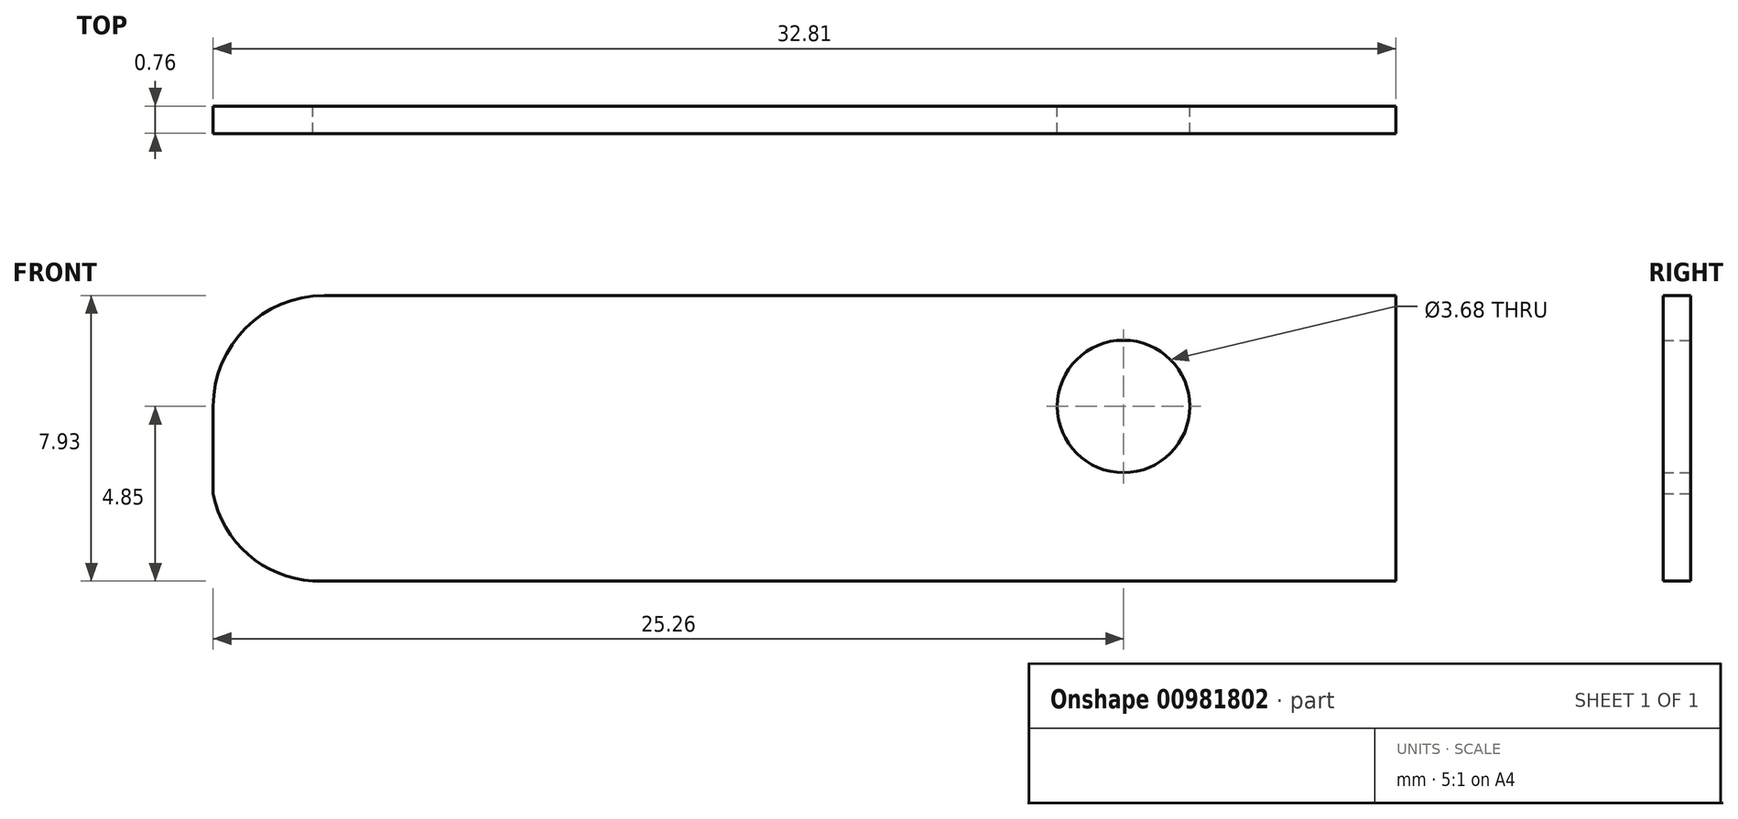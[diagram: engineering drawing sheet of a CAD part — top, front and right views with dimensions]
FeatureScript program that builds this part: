
annotation { "Feature Type Name" : "Feature", "Feature Type Description" : "" }
export const myFeature = defineFeature(function(context is Context, id is Id, definition is map)
    precondition{}
    {
        {
            var Q0;
            Q0=qCreatedBy(makeId("Front.planeOp"),FACE);
            var sketch = newSketch(context, id + "F0", { "sketchPlane" : qUnion([Q0])});
            skCircle(sketch, "E0", {"center": v(0, 0) * mm, "radius": 1.84 * mm});
            skLineSegment(sketch, "E1.bottom", {"start": v(-22.18, 3.08) * mm, "end": v(7.55, 3.08) * mm});
            skLineSegment(sketch, "E1.top", {"start": v(-22.49, -4.85) * mm, "end": v(7.55, -4.85) * mm});
            skLineSegment(sketch, "E1.left", {"start": v(-25.26, 0) * mm, "end": v(-25.26, -2.42) * mm});
            skLineSegment(sketch, "E1.right", {"start": v(7.55, 3.08) * mm, "end": v(7.55, -4.85) * mm});
            skArc(sketch, "E2", {"start": v(-22.18, 3.08) * mm, "mid": v(-24.36, 2.18) * mm, "end": v(-25.26, 0) * mm});
            skArc(sketch, "E3", {"start": v(-25.26, -2.42) * mm, "mid": v(-24.16, -4.22) * mm, "end": v(-22.15, -4.85) * mm});
            skPoint(sketch, "E4.orphan", {"position": v(-25.26, -4.85) * mm});
            skSolve(sketch);
        }
        {
            var Q0;
            Q0=makeQuery(id+"F0.imprint","IMPRINT",FACE,{"disambiguationData":[TD([[makeQuery(id+"F0.imprint","IMPRINT",EDGE,{"derivedFrom":sQuery(id+"F0.wireOp",EDGE,"E0")}),-1.0]])]});
            extrude(context, id + "F1", {"entities" : qUnion([Q0]), "depth" : 0.76 * mm, "offsetDistance" : 25.4 * mm});
        }
    });
